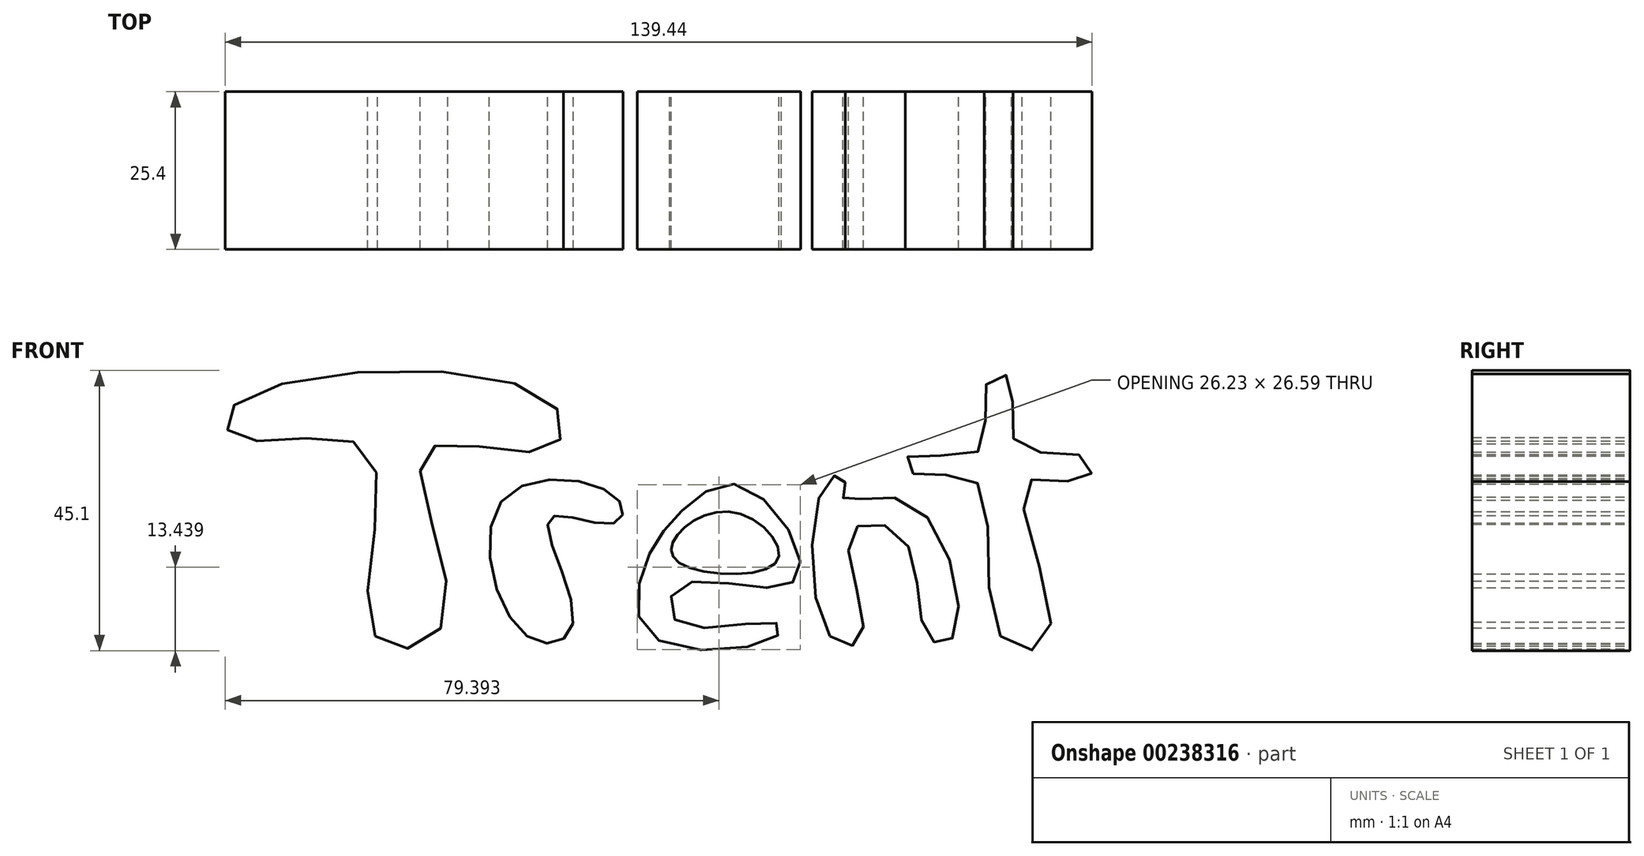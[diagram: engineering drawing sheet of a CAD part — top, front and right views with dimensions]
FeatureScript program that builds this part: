
annotation { "Feature Type Name" : "Feature", "Feature Type Description" : "" }
export const myFeature = defineFeature(function(context is Context, id is Id, definition is map)
    precondition{}
    {
        {
            var Q0;
            Q0=qCreatedBy(makeId("Front.planeOp"),FACE);
            var sketch = newSketch(context, id + "F0", { "sketchPlane" : qUnion([Q0])});
            skFitSpline(sketch, "E0", {"points": [v(-51.48, 0) * mm, v(-52.68, 29.72) * mm, v(-73.55, 31.9) * mm, v(-73.95, 37.47) * mm, v(-23.85, 38.27) * mm, v(-23.66, 30.12) * mm, v(-43.53, 29.72) * mm, v(-40.35, 2.48) * mm, v(-51.48, 0) * mm]});
            skFitSpline(sketch, "E1", {"points": [v(-27.03, 0) * mm, v(-30.81, 22.16) * mm, v(-12.52, 22.16) * mm, v(-13.12, 18.19) * mm, v(-23.46, 18.98) * mm, v(-19.68, 2.09) * mm, v(-27.03, 0) * mm]});
            skFitSpline(sketch, "E2", {"points": [v(-2.58, 11.83) * mm, v(13.12, 12.03) * mm, v(7.16, 19.78) * mm, v(-2.98, 16.2) * mm, v(-2.58, 11.83) * mm]});
            skFitSpline(sketch, "E3", {"points": [v(16.9, 12.03) * mm, v(7.16, 24.35) * mm, v(-2.58, 19.78) * mm, v(-7.95, 11.83) * mm, v(-6.96, 0) * mm, v(13.12, 0) * mm, v(13.12, 2.09) * mm, v(-2.58, 2.09) * mm, v(-2.58, 8.05) * mm, v(13.12, 7.85) * mm, v(16.9, 12.03) * mm]});
            skFitSpline(sketch, "E4", {"points": [v(21.67, 0) * mm, v(21.27, 25.15) * mm, v(24.05, 25.15) * mm, v(23.85, 22.16) * mm, v(34.79, 21.37) * mm, v(41.55, 0) * mm, v(37.37, 0) * mm, v(33.4, 15.8) * mm, v(25.05, 16.6) * mm, v(26.84, 0) * mm, v(21.67, 0) * mm]});
            skFitSpline(sketch, "E5", {"points": [v(49.1, 0) * mm, v(45.32, 24.75) * mm, v(35.18, 26.14) * mm, v(34.2, 28.92) * mm, v(45.72, 29.92) * mm, v(46.91, 40.85) * mm, v(50.69, 41.45) * mm, v(51.68, 30.91) * mm, v(62.82, 28.72) * mm, v(62.82, 25.15) * mm, v(53.07, 24.55) * mm, v(56.85, 0) * mm, v(49.1, 0) * mm]});
            skSolve(sketch);
        }
        {
            var Q0;
            Q0=makeQuery(id+"F0.imprint","IMPRINT",FACE,{"disambiguationData":[TD([[makeQuery(id+"F0.imprint","IMPRINT",EDGE,{"derivedFrom":sQuery(id+"F0.wireOp",EDGE,"E2")}),-1.0]])]});
            extrude(context, id + "F1", {"entities" : qUnion([Q0]), "depth" : 25.4 * mm});
        }
        {
            var Q0;
            Q0=makeQuery(id+"F0.imprint","IMPRINT",FACE,{"disambiguationData":[TD([[makeQuery(id+"F0.imprint","IMPRINT",EDGE,{"derivedFrom":sQuery(id+"F0.wireOp",EDGE,"E0")}),-1.0]])]});
            extrude(context, id + "F2", {"entities" : qUnion([Q0]), "depth" : 25.4 * mm});
        }
        {
            var Q0;
            Q0=makeQuery(id+"F0.imprint","IMPRINT",FACE,{"disambiguationData":[TD([[makeQuery(id+"F0.imprint","IMPRINT",EDGE,{"derivedFrom":sQuery(id+"F0.wireOp",EDGE,"E1")}),-1.0]])]});
            extrude(context, id + "F3", {"entities" : qUnion([Q0]), "depth" : 25.4 * mm});
        }
        {
            var Q0;
            Q0=makeQuery(id+"F0.imprint","IMPRINT",FACE,{"disambiguationData":[TD([[makeQuery(id+"F0.imprint","IMPRINT",EDGE,{"derivedFrom":sQuery(id+"F0.wireOp",EDGE,"E4")}),-1.0]])]});
            extrude(context, id + "F4", {"entities" : qUnion([Q0]), "depth" : 25.4 * mm});
        }
        {
            var Q0;
            Q0=makeQuery(id+"F0.imprint","IMPRINT",FACE,{"disambiguationData":[TD([[makeQuery(id+"F0.imprint","IMPRINT",EDGE,{"derivedFrom":sQuery(id+"F0.wireOp",EDGE,"E5")}),-1.0]])]});
            extrude(context, id + "F5", {"entities" : qUnion([Q0]), "depth" : 25.4 * mm});
        }
    });
